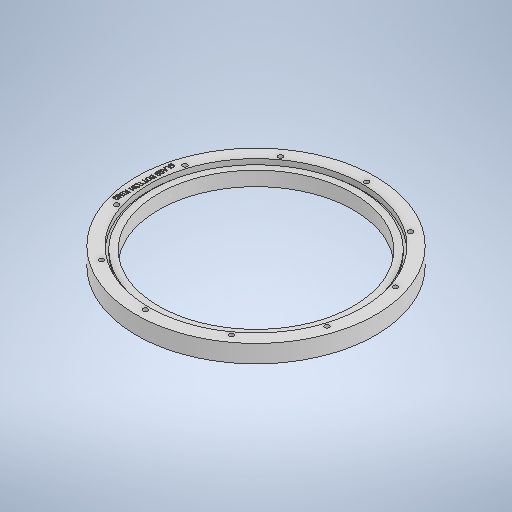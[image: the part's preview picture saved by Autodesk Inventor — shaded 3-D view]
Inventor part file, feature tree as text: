
AUTODESK INVENTOR PART (.ipt)
format: ipt  version: 2025 (Build 290162000, 162)  size: 637,440 bytes
history: native  units: mm
features: sketch x5, extrude x3, hole x1, pattern_circular x1, emboss x1
ambient origin geometry x8: Origin, YZ Plane, XZ Plane, XY Plane, X Axis, Y Axis, Z Axis, Center Point
bodies: Solid1 (feature_tree)
feature tree (11):
  extrude  "Ring"  Depth=270.0mm
  extrude  "Glass Seat"  Depth=241.0mm
  hole  "Holes"  [1 undecoded]
  pattern_circular  "Circular Pattern1"  Count=10 Angle=360.0deg
  emboss  "Emboss1"
  extrude  "Extrusion3"  Depth=241.0mm
  sketch  "Sketch1"  dims[d0=220.0mm d1=270.0mm]
  sketch  "Sketch2"  dims[d2=20.0mm d3=0.0mm d4=241.0mm]
  sketch  "Sketch3"  dims[d5=3.9mm d6=0.0mm]
  sketch  "Sketch4"  dims[d7=5.2mm d8=6.0mm d9=4.0mm d10=2.0mm d11=90.0deg d12=8.0mm d13=20.594885mm d14=125.0mm d15=100.0mm d16=360.0deg]
  sketch  "Sketch5"  dims[d18=1.0mm d19=0.0mm d21=241.0mm d22=3.0mm d23=2.5mm d24=0.0mm]
note: 1 required parameter value undecoded (feature->parameter linkage not recoverable at this tier; creation-order binding heuristic only, values carry confidence <= 0.55)
